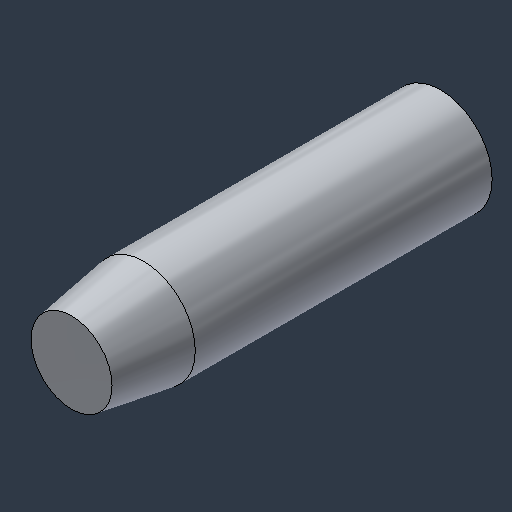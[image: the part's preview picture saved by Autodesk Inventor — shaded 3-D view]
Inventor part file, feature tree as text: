
AUTODESK INVENTOR PART (.ipt)
format: ipt  version: 2024.3 (Build 283343000, 343)  size: 108,032 bytes
history: native  units: mm (DEFAULTED — no unit token found)
features: chamfer x1
ambient origin geometry x8: Origin, YZ Plane, XZ Plane, XY Plane, X Axis, Y Axis, Z Axis, Center Point
bodies: Solid1 (feature_tree)
feature tree (1):
  chamfer  "Chamfer1"  [1 undecoded]
note: 1 required parameter value undecoded (feature->parameter linkage not recoverable at this tier; creation-order binding heuristic only, values carry confidence <= 0.55)
